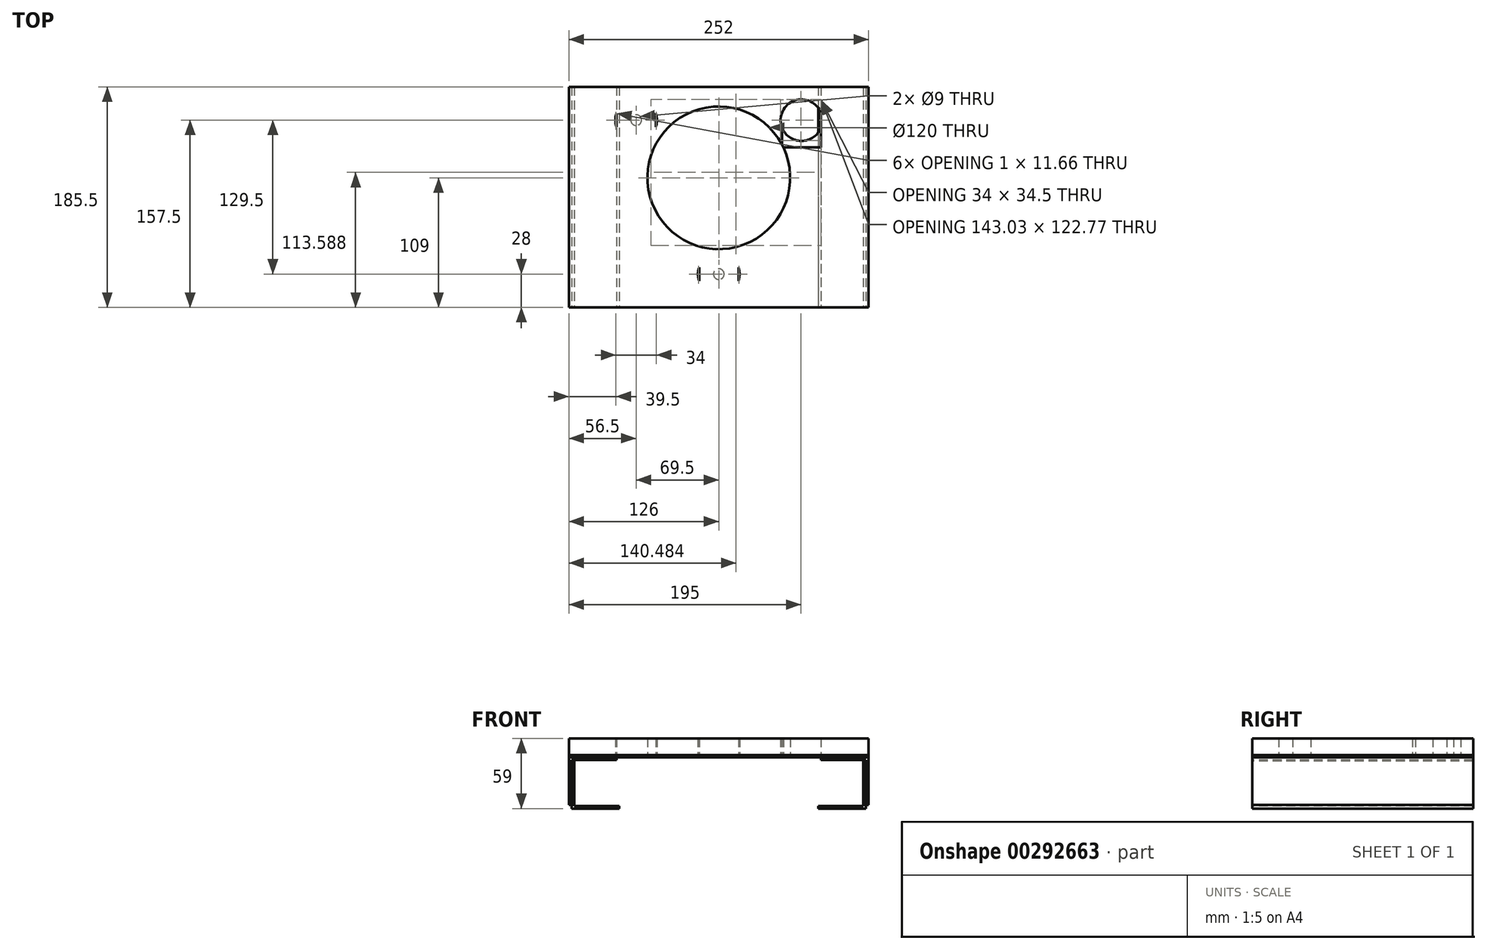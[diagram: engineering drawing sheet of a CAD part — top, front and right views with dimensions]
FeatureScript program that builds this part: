
annotation { "Feature Type Name" : "Feature", "Feature Type Description" : "" }
export const myFeature = defineFeature(function(context is Context, id is Id, definition is map)
    precondition{}
    {
        {
            var Q0;
            Q0=qCreatedBy(makeId("Top.planeOp"),FACE);
            var sketch = newSketch(context, id + "F0", { "sketchPlane" : qUnion([Q0])});
            skCircle(sketch, "E0", {"center": v(-69.5, 129.5) * mm, "radius": 17.5 * mm});
            skCircle(sketch, "E1", {"center": v(0, 0) * mm, "radius": 17.5 * mm});
            skCircle(sketch, "E2.MirrorC", {"center": v(69.5, 129.5) * mm, "radius": 17.5 * mm});
            skPoint(sketch, "E3.visualSharp", {"position": v(87, -17.5) * mm});
            skCircle(sketch, "E4", {"center": v(0, 81) * mm, "radius": 60 * mm});
            skLineSegment(sketch, "E5.bottom", {"start": v(-126, 157.5) * mm, "end": v(126, 157.5) * mm});
            skLineSegment(sketch, "E5.top", {"start": v(-126, -28) * mm, "end": v(126, -28) * mm});
            skLineSegment(sketch, "E5.left", {"start": v(-126, 157.5) * mm, "end": v(-126, -28) * mm});
            skLineSegment(sketch, "E5.right", {"start": v(126, 157.5) * mm, "end": v(126, -28) * mm});
            skLineSegment(sketch, "E6.bottom", {"start": v(53, 152.5) * mm, "end": v(86, 152.5) * mm});
            skLineSegment(sketch, "E6.top", {"start": v(53, 106.5) * mm, "end": v(86, 106.5) * mm});
            skLineSegment(sketch, "E6.left", {"start": v(53, 152.5) * mm, "end": v(53, 106.5) * mm});
            skLineSegment(sketch, "E6.right", {"start": v(86, 152.5) * mm, "end": v(86, 106.5) * mm});
            skLineSegment(sketch, "E7.MirrorCS", {"start": v(-53, 106.5) * mm, "end": v(-86, 106.5) * mm});
            skLineSegment(sketch, "E8.MirrorCS", {"start": v(-86, 152.5) * mm, "end": v(-86, 106.5) * mm});
            skLineSegment(sketch, "E9.MirrorCS", {"start": v(-53, 152.5) * mm, "end": v(-53, 106.5) * mm});
            skLineSegment(sketch, "E10.MirrorCS", {"start": v(-53, 152.5) * mm, "end": v(-86, 152.5) * mm});
            skLineSegment(sketch, "E11.bottom", {"start": v(-16.5, 23) * mm, "end": v(16.5, 23) * mm});
            skLineSegment(sketch, "E11.top", {"start": v(-16.5, -23) * mm, "end": v(16.5, -23) * mm});
            skLineSegment(sketch, "E11.left", {"start": v(-16.5, 23) * mm, "end": v(-16.5, -23) * mm});
            skLineSegment(sketch, "E11.right", {"start": v(16.5, 23) * mm, "end": v(16.5, -23) * mm});
            skSolve(sketch);
        }
        {
            var Q0;
            Q0 = qSketchRegion(id + "F0", true);
            var Q1;
            {var subQ0=sQuery(id+"F0.wireOp",EDGE,"E8.MirrorCS");var subQ1=sQuery(id+"F0.wireOp",EDGE,"E0");var subQ2=makeQuery(id+"F0.imprint","INTERSECT",VERTEX,{"disambiguationData":[OD(0.0)],"derivedFrom":[subQ1,subQ0]});Q1=makeQuery(id+"F0.imprint","IMPRINT",FACE,{"disambiguationData":[TD([[makeQuery(id+"F0.imprint","IMPRINT",EDGE,{"disambiguationData":[TD([[subQ2,-1.0]])],"derivedFrom":subQ1}),-1.0]])]});}
            var Q2;
            {var subQ0=sQuery(id+"F0.wireOp",EDGE,"E8.MirrorCS");var subQ1=sQuery(id+"F0.wireOp",EDGE,"E0");var subQ2=makeQuery(id+"F0.imprint","INTERSECT",VERTEX,{"disambiguationData":[OD(1.0)],"derivedFrom":[subQ1,subQ0]});Q2=makeQuery(id+"F0.imprint","IMPRINT",FACE,{"disambiguationData":[TD([[makeQuery(id+"F0.imprint","IMPRINT",EDGE,{"disambiguationData":[TD([[subQ2,1.0]])],"derivedFrom":subQ1}),1.0]])]});}
            var Q3;
            {var subQ3=sQuery(id+"F0.wireOp",EDGE,"E6.right");var subQ7=sQuery(id+"F0.wireOp",EDGE,"E2.MirrorC");var subQ9=makeQuery(id+"F0.imprint","INTERSECT",VERTEX,{"disambiguationData":[OD(0.0)],"derivedFrom":[subQ7,subQ3]});Q3=makeQuery(id+"F0.imprint","IMPRINT",FACE,{"disambiguationData":[TD([[makeQuery(id+"F0.imprint","IMPRINT",EDGE,{"disambiguationData":[TD([[subQ9,-1.0]])],"derivedFrom":subQ7}),1.0]])]});}
            var Q4;
            {var subQ5=sQuery(id+"F0.wireOp",EDGE,"E11.top");Q4=makeQuery(id+"F0.imprint","IMPRINT",FACE,{"disambiguationData":[TD([[makeQuery(id+"F0.imprint","IMPRINT",EDGE,{"derivedFrom":subQ5}),1.0]])]});}
            var Q5;
            {var subQ0=sQuery(id+"F0.wireOp",EDGE,"E6.right");var subQ1=sQuery(id+"F0.wireOp",EDGE,"E2.MirrorC");var subQ2=makeQuery(id+"F0.imprint","INTERSECT",VERTEX,{"disambiguationData":[OD(0.0)],"derivedFrom":[subQ1,subQ0]});Q5=makeQuery(id+"F0.imprint","IMPRINT",FACE,{"disambiguationData":[TD([[makeQuery(id+"F0.imprint","IMPRINT",EDGE,{"disambiguationData":[TD([[subQ2,-1.0]])],"derivedFrom":subQ1}),-1.0]])]});}
            var Q6;
            {var subQ5=sQuery(id+"F0.wireOp",EDGE,"E10.MirrorCS");Q6=makeQuery(id+"F0.imprint","IMPRINT",FACE,{"disambiguationData":[TD([[makeQuery(id+"F0.imprint","IMPRINT",EDGE,{"derivedFrom":subQ5}),1.0]])]});}
            var Q7;
            {var subQ0=sQuery(id+"F0.wireOp",EDGE,"E11.right");var subQ1=sQuery(id+"F0.wireOp",EDGE,"E1");var subQ2=makeQuery(id+"F0.imprint","INTERSECT",VERTEX,{"disambiguationData":[OD(1.0)],"derivedFrom":[subQ1,subQ0]});Q7=makeQuery(id+"F0.imprint","IMPRINT",FACE,{"disambiguationData":[TD([[makeQuery(id+"F0.imprint","IMPRINT",EDGE,{"disambiguationData":[TD([[subQ2,-1.0]])],"derivedFrom":subQ1}),1.0]])]});}
            var Q8;
            {var subQ5=sQuery(id+"F0.wireOp",EDGE,"E6.bottom");Q8=makeQuery(id+"F0.imprint","IMPRINT",FACE,{"disambiguationData":[TD([[makeQuery(id+"F0.imprint","IMPRINT",EDGE,{"derivedFrom":subQ5}),-1.0]])]});}
            var Q9;
            {var subQ0=sQuery(id+"F0.wireOp",EDGE,"E2.MirrorC");var subQ1=makeQuery(id+"F0.imprint","IMPRINT",VERTEX,{"derivedFrom":subQ0});Q9=makeQuery(id+"F0.imprint","IMPRINT",FACE,{"disambiguationData":[TD([[makeQuery(id+"F0.imprint","IMPRINT",EDGE,{"disambiguationData":[TD([[subQ1,1.0]])],"derivedFrom":subQ0}),-1.0]])]});}
            var Q10;
            {var subQ0=sQuery(id+"F0.wireOp",EDGE,"E8.MirrorCS");var subQ1=sQuery(id+"F0.wireOp",EDGE,"E0");var subQ2=makeQuery(id+"F0.imprint","INTERSECT",VERTEX,{"disambiguationData":[OD(0.0)],"derivedFrom":[subQ1,subQ0]});Q10=makeQuery(id+"F0.imprint","IMPRINT",FACE,{"disambiguationData":[TD([[makeQuery(id+"F0.imprint","IMPRINT",EDGE,{"disambiguationData":[TD([[subQ2,1.0]])],"derivedFrom":subQ1}),1.0]])]});}
            var Q11;
            {var subQ5=sQuery(id+"F0.wireOp",EDGE,"E11.right");var subQ8=sQuery(id+"F0.wireOp",EDGE,"E1");var subQ9=makeQuery(id+"F0.imprint","INTERSECT",VERTEX,{"disambiguationData":[OD(1.0)],"derivedFrom":[subQ8,subQ5]});Q11=makeQuery(id+"F0.imprint","IMPRINT",FACE,{"disambiguationData":[TD([[makeQuery(id+"F0.imprint","IMPRINT",EDGE,{"disambiguationData":[TD([[subQ9,-1.0]])],"derivedFrom":subQ8}),-1.0]])]});}
            var Q12;
            {var subQ0=sQuery(id+"F0.wireOp",EDGE,"E6.right");var subQ1=sQuery(id+"F0.wireOp",EDGE,"E2.MirrorC");var subQ2=makeQuery(id+"F0.imprint","INTERSECT",VERTEX,{"disambiguationData":[OD(0.0)],"derivedFrom":[subQ1,subQ0]});Q12=makeQuery(id+"F0.imprint","IMPRINT",FACE,{"disambiguationData":[TD([[makeQuery(id+"F0.imprint","IMPRINT",EDGE,{"disambiguationData":[TD([[subQ2,1.0]])],"derivedFrom":subQ1}),-1.0]])]});}
            var Q13;
            {var subQ0=sQuery(id+"F0.wireOp",EDGE,"E1");var subQ1=makeQuery(id+"F0.imprint","IMPRINT",VERTEX,{"derivedFrom":subQ0});Q13=makeQuery(id+"F0.imprint","IMPRINT",FACE,{"disambiguationData":[TD([[makeQuery(id+"F0.imprint","IMPRINT",EDGE,{"disambiguationData":[TD([[subQ1,-1.0]])],"derivedFrom":subQ0}),1.0]])]});}
            var Q14;
            {var subQ0=sQuery(id+"F0.wireOp",EDGE,"E0");var subQ1=makeQuery(id+"F0.imprint","IMPRINT",VERTEX,{"derivedFrom":subQ0});Q14=makeQuery(id+"F0.imprint","IMPRINT",FACE,{"disambiguationData":[TD([[makeQuery(id+"F0.imprint","IMPRINT",EDGE,{"disambiguationData":[TD([[subQ1,1.0]])],"derivedFrom":subQ0}),1.0]])]});}
            var Q15;
            {var subQ0=sQuery(id+"F0.wireOp",EDGE,"E11.left");var subQ1=sQuery(id+"F0.wireOp",EDGE,"E1");var subQ2=makeQuery(id+"F0.imprint","INTERSECT",VERTEX,{"disambiguationData":[OD(0.0)],"derivedFrom":[subQ1,subQ0]});Q15=makeQuery(id+"F0.imprint","IMPRINT",FACE,{"disambiguationData":[TD([[makeQuery(id+"F0.imprint","IMPRINT",EDGE,{"disambiguationData":[TD([[subQ2,1.0]])],"derivedFrom":subQ1}),1.0]])]});}
            extrude(context, id + "F1", {"entities" : qUnion([Q0, Q1, Q2, Q3, Q4, Q5, Q6, Q7, Q8, Q9, Q10, Q11, Q12, Q13, Q14, Q15]), "depth" : 2 * mm, "offsetDistance" : 25 * mm});
        }
        {
            var Q0;
            Q0=qCreatedBy(makeId("Front.planeOp"),FACE);
            var sketch = newSketch(context, id + "F2", { "sketchPlane" : qUnion([Q0])});
            skLineSegment(sketch, "E12", {"start": v(-126, 0) * mm, "end": v(-86, 0) * mm});
            skLineSegment(sketch, "E13", {"start": v(-126, 0) * mm, "end": v(-126, -40) * mm});
            skLineSegment(sketch, "E14", {"start": v(-126, -40) * mm, "end": v(-123.75, -40) * mm});
            skLineSegment(sketch, "E15", {"start": v(-86, 0) * mm, "end": v(-86, -2.25) * mm});
            skLineSegment(sketch, "E16", {"start": v(-86, -2.25) * mm, "end": v(-123.75, -2.25) * mm});
            skLineSegment(sketch, "E17", {"start": v(-123.75, -2.25) * mm, "end": v(-123.75, -40) * mm});
            skLineSegment(sketch, "E18.MirrorCS", {"start": v(86, 0) * mm, "end": v(86, -2.25) * mm});
            skLineSegment(sketch, "E19.MirrorCS", {"start": v(126, -40) * mm, "end": v(123.75, -40) * mm});
            skLineSegment(sketch, "E20.MirrorCS", {"start": v(126, 0) * mm, "end": v(86, 0) * mm});
            skLineSegment(sketch, "E21.MirrorCS", {"start": v(126, 0) * mm, "end": v(126, -40) * mm});
            skLineSegment(sketch, "E22.MirrorCS", {"start": v(123.75, -2.25) * mm, "end": v(123.75, -40) * mm});
            skLineSegment(sketch, "E23.MirrorCS", {"start": v(86, -2.25) * mm, "end": v(123.75, -2.25) * mm});
            skSolve(sketch);
        }
        {
            var Q0;
            Q0 = qSketchRegion(id + "F2", true);
            var Q1;
            Q1=makeQuery(id+"F1.opExtrude","SWEPT_FACE",FACE,{"disambiguationData":[OSD([sQuery(id+"F0.wireOp",EDGE,"E5.bottom")])]});
            var Q2;
            Q2=makeQuery(id+"F1.opExtrude","SWEPT_FACE",FACE,{"disambiguationData":[OSD([sQuery(id+"F0.wireOp",EDGE,"E5.top")])]});
            extrude(context, id + "F3", {"entities" : qUnion([Q0]), "endBound" : BoundingType.UP_TO_SURFACE, "oppositeDirection" : true, "depth" : 25 * mm, "endBoundEntityFace" : qUnion([Q1]), "offsetDistance" : 25 * mm, "hasSecondDirection" : true, "secondDirectionBound" : SecondDirectionBoundingType.UP_TO_SURFACE, "secondDirectionOppositeDirection" : false, "secondDirectionDepth" : 25 * mm, "secondDirectionBoundEntityFace" : qUnion([Q2])});
        }
        {
            var Q0;
            Q0=makeQuery(id+"F3.opExtrude","SWEPT_BODY",BODY,{"disambiguationData":[OSD([sQuery(id+"F2.wireOp",EDGE,"E12"),sQuery(id+"F2.wireOp",EDGE,"E13"),sQuery(id+"F2.wireOp",EDGE,"E14"),sQuery(id+"F2.wireOp",EDGE,"E15"),sQuery(id+"F2.wireOp",EDGE,"E16"),sQuery(id+"F2.wireOp",EDGE,"E17")])]});
            var Q1;
            Q1=makeQuery(id+"F3.opExtrude","SWEPT_BODY",BODY,{"disambiguationData":[OSD([sQuery(id+"F2.wireOp",EDGE,"E18.MirrorCS"),sQuery(id+"F2.wireOp",EDGE,"E19.MirrorCS"),sQuery(id+"F2.wireOp",EDGE,"E20.MirrorCS"),sQuery(id+"F2.wireOp",EDGE,"E21.MirrorCS"),sQuery(id+"F2.wireOp",EDGE,"E22.MirrorCS"),sQuery(id+"F2.wireOp",EDGE,"E23.MirrorCS")])]});
            var Q2;
            Q2=makeQuery(id+"F3.opExtrude","SWEPT_FACE",FACE,{"disambiguationData":[OSD([sQuery(id+"F2.wireOp",EDGE,"E19.MirrorCS")])]});
            mirror(context, id + "F4", {"entities" : qUnion([Q0, Q1]), "mirrorPlane" : qUnion([Q2])});
        }
        {
            var Q0;
            Q0=makeQuery(id+"F4.opPattern","COPY",BODY,{"derivedFrom":makeQuery(id+"F3.opExtrude","SWEPT_BODY",BODY,{"disambiguationData":[OSD([sQuery(id+"F2.wireOp",EDGE,"E12"),sQuery(id+"F2.wireOp",EDGE,"E13"),sQuery(id+"F2.wireOp",EDGE,"E14"),sQuery(id+"F2.wireOp",EDGE,"E15"),sQuery(id+"F2.wireOp",EDGE,"E16"),sQuery(id+"F2.wireOp",EDGE,"E17")])]}),"instanceName":"1"});
            transform(context, id + "F5", {"entities" : qUnion([Q0]), "transformType" : TransformType.TRANSLATION_3D, "dx" : 2.25 * mm, "dy" : 0 * mm, "dz" : 37 * mm, "makeCopy" : false});
        }
        {
            var Q0;
            Q0=makeQuery(id+"F4.opPattern","COPY",BODY,{"derivedFrom":makeQuery(id+"F3.opExtrude","SWEPT_BODY",BODY,{"disambiguationData":[OSD([sQuery(id+"F2.wireOp",EDGE,"E18.MirrorCS"),sQuery(id+"F2.wireOp",EDGE,"E19.MirrorCS"),sQuery(id+"F2.wireOp",EDGE,"E20.MirrorCS"),sQuery(id+"F2.wireOp",EDGE,"E21.MirrorCS"),sQuery(id+"F2.wireOp",EDGE,"E22.MirrorCS"),sQuery(id+"F2.wireOp",EDGE,"E23.MirrorCS")])]}),"instanceName":"1"});
            deleteBodies(context, id + "F6", {"entities" : qUnion([Q0])});
        }
        {
            var Q0;
            Q0=makeQuery(id+"F4.opPattern","COPY",BODY,{"derivedFrom":makeQuery(id+"F3.opExtrude","SWEPT_BODY",BODY,{"disambiguationData":[OSD([sQuery(id+"F2.wireOp",EDGE,"E12"),sQuery(id+"F2.wireOp",EDGE,"E13"),sQuery(id+"F2.wireOp",EDGE,"E14"),sQuery(id+"F2.wireOp",EDGE,"E15"),sQuery(id+"F2.wireOp",EDGE,"E16"),sQuery(id+"F2.wireOp",EDGE,"E17")])]}),"instanceName":"1"});
            var Q1;
            Q1=qCreatedBy(makeId("Right.planeOp"),FACE);
            mirror(context, id + "F7", {"entities" : qUnion([Q0]), "mirrorPlane" : qUnion([Q1])});
        }
        {
            var Q0;
            {var subQ5=sQuery(id+"F0.wireOp",EDGE,"E11.top");Q0=makeQuery(id+"F0.imprint","IMPRINT",FACE,{"disambiguationData":[TD([[makeQuery(id+"F0.imprint","IMPRINT",EDGE,{"derivedFrom":subQ5}),1.0]])]});}
            var Q1;
            {var subQ0=sQuery(id+"F0.wireOp",EDGE,"E11.right");var subQ1=sQuery(id+"F0.wireOp",EDGE,"E1");var subQ2=makeQuery(id+"F0.imprint","INTERSECT",VERTEX,{"disambiguationData":[OD(1.0)],"derivedFrom":[subQ1,subQ0]});Q1=makeQuery(id+"F0.imprint","IMPRINT",FACE,{"disambiguationData":[TD([[makeQuery(id+"F0.imprint","IMPRINT",EDGE,{"disambiguationData":[TD([[subQ2,-1.0]])],"derivedFrom":subQ1}),1.0]])]});}
            var Q2;
            {var subQ5=sQuery(id+"F0.wireOp",EDGE,"E11.right");var subQ8=sQuery(id+"F0.wireOp",EDGE,"E1");var subQ9=makeQuery(id+"F0.imprint","INTERSECT",VERTEX,{"disambiguationData":[OD(1.0)],"derivedFrom":[subQ8,subQ5]});Q2=makeQuery(id+"F0.imprint","IMPRINT",FACE,{"disambiguationData":[TD([[makeQuery(id+"F0.imprint","IMPRINT",EDGE,{"disambiguationData":[TD([[subQ9,-1.0]])],"derivedFrom":subQ8}),-1.0]])]});}
            var Q3;
            {var subQ0=sQuery(id+"F0.wireOp",EDGE,"E8.MirrorCS");var subQ1=sQuery(id+"F0.wireOp",EDGE,"E0");var subQ2=makeQuery(id+"F0.imprint","INTERSECT",VERTEX,{"disambiguationData":[OD(0.0)],"derivedFrom":[subQ1,subQ0]});Q3=makeQuery(id+"F0.imprint","IMPRINT",FACE,{"disambiguationData":[TD([[makeQuery(id+"F0.imprint","IMPRINT",EDGE,{"disambiguationData":[TD([[subQ2,-1.0]])],"derivedFrom":subQ1}),-1.0]])]});}
            var Q4;
            {var subQ0=sQuery(id+"F0.wireOp",EDGE,"E8.MirrorCS");var subQ1=sQuery(id+"F0.wireOp",EDGE,"E0");var subQ2=makeQuery(id+"F0.imprint","INTERSECT",VERTEX,{"disambiguationData":[OD(1.0)],"derivedFrom":[subQ1,subQ0]});Q4=makeQuery(id+"F0.imprint","IMPRINT",FACE,{"disambiguationData":[TD([[makeQuery(id+"F0.imprint","IMPRINT",EDGE,{"disambiguationData":[TD([[subQ2,1.0]])],"derivedFrom":subQ1}),1.0]])]});}
            var Q5;
            {var subQ5=sQuery(id+"F0.wireOp",EDGE,"E10.MirrorCS");Q5=makeQuery(id+"F0.imprint","IMPRINT",FACE,{"disambiguationData":[TD([[makeQuery(id+"F0.imprint","IMPRINT",EDGE,{"derivedFrom":subQ5}),1.0]])]});}
            var Q6;
            {var subQ3=sQuery(id+"F0.wireOp",EDGE,"E6.right");var subQ7=sQuery(id+"F0.wireOp",EDGE,"E2.MirrorC");var subQ9=makeQuery(id+"F0.imprint","INTERSECT",VERTEX,{"disambiguationData":[OD(0.0)],"derivedFrom":[subQ7,subQ3]});Q6=makeQuery(id+"F0.imprint","IMPRINT",FACE,{"disambiguationData":[TD([[makeQuery(id+"F0.imprint","IMPRINT",EDGE,{"disambiguationData":[TD([[subQ9,-1.0]])],"derivedFrom":subQ7}),1.0]])]});}
            var Q7;
            {var subQ0=sQuery(id+"F0.wireOp",EDGE,"E6.right");var subQ1=sQuery(id+"F0.wireOp",EDGE,"E2.MirrorC");var subQ2=makeQuery(id+"F0.imprint","INTERSECT",VERTEX,{"disambiguationData":[OD(0.0)],"derivedFrom":[subQ1,subQ0]});Q7=makeQuery(id+"F0.imprint","IMPRINT",FACE,{"disambiguationData":[TD([[makeQuery(id+"F0.imprint","IMPRINT",EDGE,{"disambiguationData":[TD([[subQ2,-1.0]])],"derivedFrom":subQ1}),-1.0]])]});}
            var Q8;
            {var subQ5=sQuery(id+"F0.wireOp",EDGE,"E6.bottom");Q8=makeQuery(id+"F0.imprint","IMPRINT",FACE,{"disambiguationData":[TD([[makeQuery(id+"F0.imprint","IMPRINT",EDGE,{"derivedFrom":subQ5}),-1.0]])]});}
            extrude(context, id + "F8", {"entities" : qUnion([Q0, Q1, Q2, Q3, Q4, Q5, Q6, Q7, Q8]), "depth" : 16 * mm, "offsetDistance" : 25 * mm});
        }
        {
            var Q0;
            Q0=sQuery(id+"F0.wireOp",VERTEX,"E0.center");
            var Q1;
            Q1=sQuery(id+"F0.wireOp",VERTEX,"E2.MirrorC.center");
            var Q2;
            Q2=sQuery(id+"F0.wireOp",VERTEX,"E1.center");
            var Q3;
            Q3=makeQuery(id+"F1.opExtrude","SWEPT_BODY",BODY,{"disambiguationData":[OSD([sQuery(id+"F0.wireOp",EDGE,"E4"),sQuery(id+"F0.wireOp",EDGE,"E5.bottom"),sQuery(id+"F0.wireOp",EDGE,"E5.top"),sQuery(id+"F0.wireOp",EDGE,"E5.left"),sQuery(id+"F0.wireOp",EDGE,"E5.right")])]});
            hole(context, id + "F9", {"style" : HoleStyle.SIMPLE, "endStyle" : HoleEndStyle.THROUGH, "oppositeDirection" : true, "standardTappedOrClearance" : lookupTablePath({ "fit" : "Normal", "standard" : "ISO", "size" : "M8", "type" : "Clearance" }), "standardBlindInLast" : lookupTablePath({ "fit" : "Normal", "standard" : "ISO", "engagement" : "75%", "pitch" : "1.25 mm", "size" : "M8", "type" : "Clearance & tapped" }), "holeDiameter" : 9 * mm, "majorDiameter" : 6 * mm, "isTappedThrough" : true, "tappedDepth" : 12 * mm, "tapClearance" : 3, "locations" : qUnion([Q0, Q1, Q2]), "scope" : qUnion([Q3])});
        }
    });
